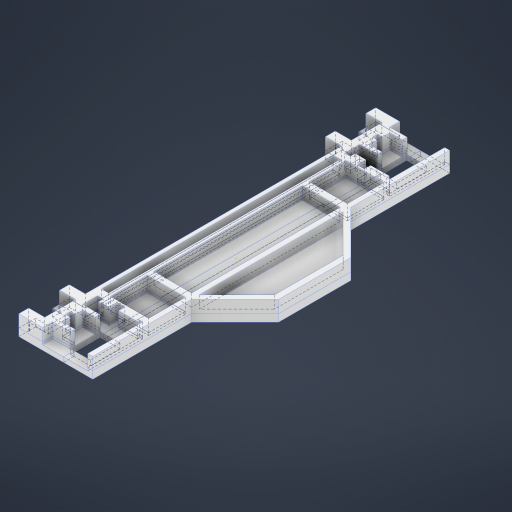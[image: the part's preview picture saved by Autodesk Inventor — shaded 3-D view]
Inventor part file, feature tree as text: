
AUTODESK INVENTOR PART (.ipt)
format: ipt  version: 2024 (Build 280153000, 153)  size: 979,968 bytes
history: native  units: mm
features: sketch x26, extrude x24, projected_geometry x8, chamfer x2, other x1
ambient origin geometry x8: Origin, YZ Plane, XZ Plane, XY Plane, X Axis, Y Axis, Z Axis, Center Point
bodies: Body1 (feature_tree)
feature tree (61):
  other  "Твердое тело1"
  extrude  "Выдавливание1"  Depth=722.0mm
  extrude  "Выдавливание2"  Depth=21.0mm
  extrude  "Выдавливание3"  Depth=60.0mm
  extrude  "Выдавливание4"  Depth=10.0mm TaperAngle=0.0deg
  extrude  "Выдавливание5"  Depth=500.0mm
  extrude  "Выдавливание6"  Depth=25.0mm TaperAngle=0.0deg
  extrude  "Выдавливание7"  TaperAngle=0.0deg  [1 undecoded]
  extrude  "Выдавливание8"  Depth=20.0mm
  chamfer  "Фаска1"  Distance=40.0mm
  extrude  "Выдавливание9"  Depth=200.0mm
  extrude  "Выдавливание11"  Depth=42.0mm
  sketch  "Sketch13"  dims[d0=87.0mm d1=722.0mm]
  chamfer  "Chamfer2"  Distance=10.0mm
  extrude  "Extrusion12"  Depth=8.0mm
  extrude  "Extrusion13"  Depth=8.0mm
  extrude  "Extrusion14"  Depth=8.0mm
  extrude  "Extrusion15"  Depth=19.0mm
  extrude  "Extrusion16"  Depth=34.0mm
  extrude  "Extrusion18"  Depth=20.0mm TaperAngle=0.0deg
  extrude  "Extrusion19"  Depth=12.0mm TaperAngle=45.0deg
  extrude  "Extrusion20"  Depth=5.0mm
  sketch  "Sketch22"  dims[d25=200.0mm d26=200.0mm]
  extrude  "Extrusion21"  Depth=5.0mm
  extrude  "Extrusion22"  Depth=19.0mm
  extrude  "Extrusion26"  Depth=19.0mm
  extrude  "Extrusion27"  Depth=2.0mm TaperAngle=0.0deg
  extrude  "Extrusion28"  Depth=10.0mm
  extrude  "Extrusion29"  Depth=20.0mm
  sketch  "Эскиз1"
  sketch  "Эскиз2"
  sketch  "Эскиз3"
  sketch  "Эскиз4"
  sketch  "Эскиз6"
  sketch  "Эскиз7"
  sketch  "Эскиз8"
  sketch  "Эскиз9"
  projected_geometry  "Спроецированная петля1"
  sketch  "Эскиз10"
  projected_geometry  "Спроецированная петля2"
  projected_geometry  "Спроецированная петля3"
  sketch  "Эскиз12"
  sketch  "Sketch14"  dims[d2=10.0mm d3=0.0mm d4=21.0mm]
  sketch  "Sketch15"  dims[d5=16.0mm d6=60.0mm]
  sketch  "Sketch16"  dims[d7=40.0mm d8=10.0mm d9=0.0mm]
  sketch  "Sketch17"  dims[d10=10.0mm d12=500.0mm]
  sketch  "Sketch18"  dims[d13=111.0mm d14=25.0mm d15=0.0mm]
  sketch  "Sketch19"  dims[d16=722.0mm d17=0.0mm]
  sketch  "Sketch20"  dims[d18=35.0mm d19=0.0mm d20=20.0mm]
  sketch  "Sketch21"  dims[d22=10.0mm d23=40.0mm d24=0.0mm]
  projected_geometry  "Projected Loop6"
  sketch  "Sketch23"  dims[d27=5.0mm d28=0.0mm d29=42.0mm]
  projected_geometry  "Projected Loop7"
  sketch  "Sketch24"  dims[d30=70.0mm]
  projected_geometry  "Projected Loop8"
  projected_geometry  "Projected Loop9"
  sketch  "Sketch28"  dims[d31=326.0mm]
  sketch  "Sketch30"  dims[d32=5.0mm]
  sketch  "Sketch31"  dims[d33=10.5mm d34=10.0mm d35=0.0mm]
  sketch  "Sketch32"  dims[d36=4.25mm d37=4.25mm d38=4.25mm d39=4.25mm d40=19.0mm d41=34.0mm d42=20.0mm d43=0.0mm d44=12.0mm d45=2.0mm d46=45.0deg d47=5.0mm d48=5.0mm d49=19.0mm d50=19.0mm d51=2.0mm d52=0.0mm d56=10.0mm d57=20.0mm d58=5.0mm d59=25.0mm d60=0.0mm d61=42.0mm d62=70.0mm d63=5.0mm d64=10.5mm d65=5.0mm d66=5.0mm d67=19.0mm d68=19.0mm d69=19.0mm d70=34.0mm d71=88.0mm d72=2.0mm d73=45.0deg d75=11.0mm d76=40.0mm d77=0.0mm d78=11.0mm d79=11.0mm d80=2.0mm d81=0.0mm d82=10.0mm d83=0.0mm d84=0.0mm d85=0.0mm d86=722.0mm d87=361.0mm d88=21.0mm d89=13.0mm d90=34.0mm d91=32.5mm d92=13.0mm d93=7.0mm d94=5.736667mm d95=5.736897mm d96=15.0mm d97=0.0mm d100=10.0mm d101=0.0mm d102=10.0mm d103=0.0mm d104=20.0mm d105=20.0mm d106=10.0mm d107=10.0mm d108=722.0mm d109=361.0mm d110=30.0mm d111=0.0mm d112=16.0mm d113=16.0mm d114=16.0mm d115=16.0mm d116=5.0mm d117=0.0mm d118=30.0mm d119=0.0mm d131=10.0mm d132=0.0mm d133=0.05mm d134=5.0mm d135=5.0mm d136=1000.0mm d137=0.0mm d138=0.05mm d140=2.0mm d141=1000.0mm d142=0.0mm d143=16.0mm d144=16.0mm d145=8.0mm d146=8.0mm d147=1000.0mm d148=0.0mm]
  projected_geometry  "Projected Loop10"
note: 1 required parameter value undecoded (feature->parameter linkage not recoverable at this tier; creation-order binding heuristic only, values carry confidence <= 0.55)
